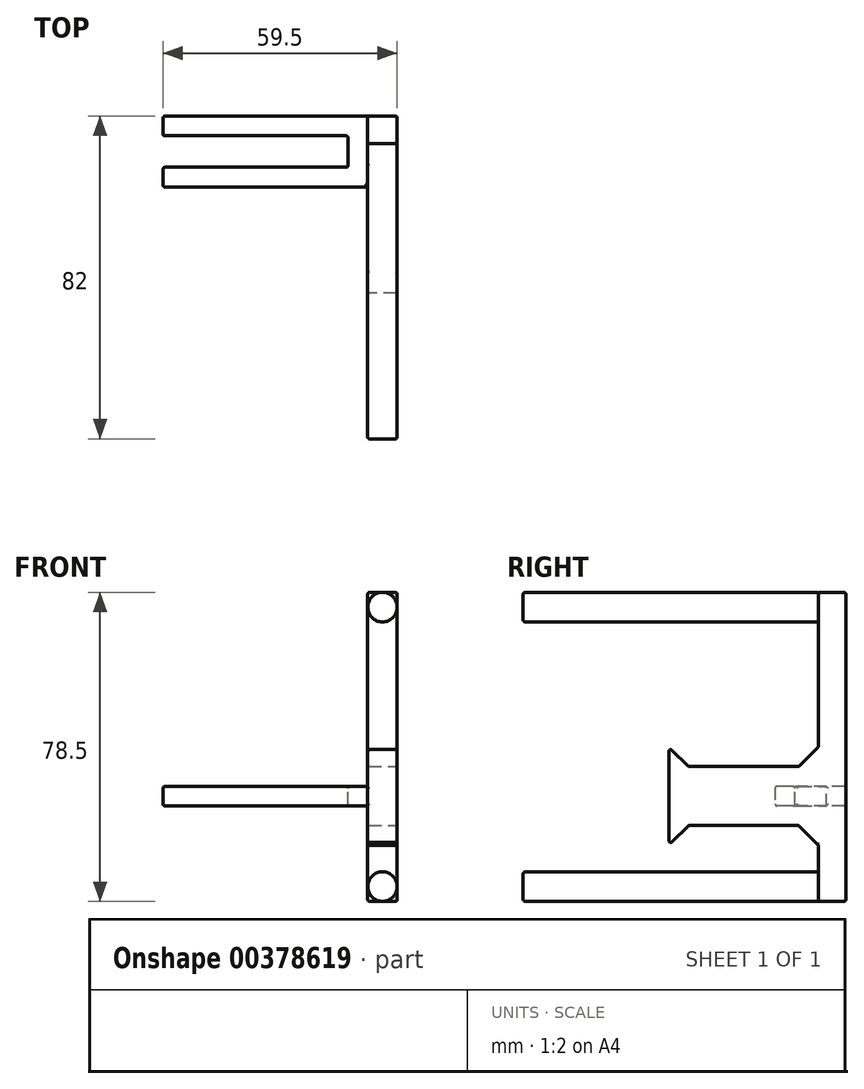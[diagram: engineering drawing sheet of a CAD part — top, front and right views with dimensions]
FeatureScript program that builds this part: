
annotation { "Feature Type Name" : "Feature", "Feature Type Description" : "" }
export const myFeature = defineFeature(function(context is Context, id is Id, definition is map)
    precondition{}
    {
        {
            var Q0;
            Q0=qCreatedBy(makeId("Front.planeOp"),FACE);
            var sketch = newSketch(context, id + "F0", { "sketchPlane" : qUnion([Q0])});
            skLineSegment(sketch, "E0", {"start": v(0, 35.5) * mm, "end": v(0, -35.5) * mm, "construction": true});
            skCircle(sketch, "E1", {"center": v(0, 35.5) * mm, "radius": 3.75 * mm});
            skCircle(sketch, "E2.MirrorC", {"center": v(0, -35.5) * mm, "radius": 3.75 * mm});
            skSolve(sketch);
        }
        {
            var Q0;
            Q0 = qSketchRegion(id + "F0", true);
            extrude(context, id + "F1", {"entities" : qUnion([Q0]), "depth" : 75 * mm});
        }
        {
            var Q0;
            Q0=qCreatedBy(makeId("Front.planeOp"),FACE);
            var sketch = newSketch(context, id + "F2", { "sketchPlane" : qUnion([Q0])});
            skLineSegment(sketch, "E3.bottom", {"start": v(3.75, 39.25) * mm, "end": v(-3.75, 39.25) * mm});
            skLineSegment(sketch, "E3.top", {"start": v(3.75, -39.25) * mm, "end": v(-3.75, -39.25) * mm});
            skLineSegment(sketch, "E3.left", {"start": v(3.75, 39.25) * mm, "end": v(3.75, -39.25) * mm});
            skLineSegment(sketch, "E3.right", {"start": v(-3.75, 39.25) * mm, "end": v(-3.75, -39.25) * mm});
            skSolve(sketch);
        }
        {
            var Q0;
            Q0 = qSketchRegion(id + "F2", true);
            extrude(context, id + "F3", {"entities" : qUnion([Q0]), "oppositeDirection" : true, "depth" : 7 * mm});
        }
        {
            var Q0;
            Q0=makeQuery(id+"F3.opExtrude","CAP_FACE",FACE,{"disambiguationData":[OSD([sQuery(id+"F2.wireOp",EDGE,"E3.bottom"),sQuery(id+"F2.wireOp",EDGE,"E3.top"),sQuery(id+"F2.wireOp",EDGE,"E3.left"),sQuery(id+"F2.wireOp",EDGE,"E3.right")])],"isStart":false});
            var sketch = newSketch(context, id + "F4", { "sketchPlane" : qUnion([Q0])});
            skLineSegment(sketch, "E4.bottom", {"start": v(-3.75, 0) * mm, "end": v(3.75, 0) * mm});
            skLineSegment(sketch, "E4.top", {"start": v(-3.75, -25) * mm, "end": v(3.75, -25) * mm});
            skLineSegment(sketch, "E4.left", {"start": v(-3.75, 0) * mm, "end": v(-3.75, -25) * mm});
            skLineSegment(sketch, "E4.right", {"start": v(3.75, 0) * mm, "end": v(3.75, -25) * mm});
            skSolve(sketch);
        }
        {
            var Q0;
            Q0 = qSketchRegion(id + "F4", true);
            extrude(context, id + "F5", {"entities" : qUnion([Q0]), "operationType" : NewBodyOperationType.ADD, "oppositeDirection" : true, "depth" : 45 * mm});
        }
        {
            var Q0;
            Q0=makeQuery(id+"F5.boolean.opBoolean","MERGE",FACE,{"derivedFrom":[makeQuery(id+"F3.opExtrude","SWEPT_FACE",FACE,{"disambiguationData":[OSD([sQuery(id+"F2.wireOp",EDGE,"E3.left")])]}),makeQuery(id+"F5.opExtrude","SWEPT_FACE",FACE,{"disambiguationData":[OSD([sQuery(id+"F4.wireOp",EDGE,"E4.left")])]})]});
            var sketch = newSketch(context, id + "F6", { "sketchPlane" : qUnion([Q0])});
            skLineSegment(sketch, "E5", {"start": v(-38, 0) * mm, "end": v(-33, -5) * mm});
            skLineSegment(sketch, "E6", {"start": v(-33, -5) * mm, "end": v(-5, -5) * mm});
            skLineSegment(sketch, "E7", {"start": v(-5, -5) * mm, "end": v(0, 0) * mm});
            skLineSegment(sketch, "E8", {"start": v(-38, -12.5) * mm, "end": v(7, -12.5) * mm, "construction": true});
            skLineSegment(sketch, "E9.MirrorCS", {"start": v(-38, -25) * mm, "end": v(-33, -20) * mm});
            skLineSegment(sketch, "E10.MirrorCS", {"start": v(-33, -20) * mm, "end": v(-5, -20) * mm});
            skLineSegment(sketch, "E11.MirrorCS", {"start": v(-5, -20) * mm, "end": v(0, -25) * mm});
            skLineSegment(sketch, "E12", {"start": v(-38, 0) * mm, "end": v(0, 0) * mm});
            skLineSegment(sketch, "E13", {"start": v(0, -25) * mm, "end": v(-38, -25) * mm});
            skSolve(sketch);
        }
        {
            var Q0;
            Q0 = qSketchRegion(id + "F6", true);
            var Q1;
            Q1=makeQuery(id+"F5.boolean.opBoolean","MERGE",FACE,{"derivedFrom":[makeQuery(id+"F3.opExtrude","SWEPT_FACE",FACE,{"disambiguationData":[OSD([sQuery(id+"F2.wireOp",EDGE,"E3.right")])]}),makeQuery(id+"F5.opExtrude","SWEPT_FACE",FACE,{"disambiguationData":[OSD([sQuery(id+"F4.wireOp",EDGE,"E4.right")])]})]});
            extrude(context, id + "F7", {"entities" : qUnion([Q0]), "operationType" : NewBodyOperationType.REMOVE, "oppositeDirection" : true, "endBoundEntityFace" : qUnion([Q1]), "depth" : 25 * mm});
        }
        {
            var Q0;
            Q0=makeQuery(id+"F5.boolean.opBoolean","MERGE",FACE,{"derivedFrom":[makeQuery(id+"F3.opExtrude","SWEPT_FACE",FACE,{"disambiguationData":[OSD([sQuery(id+"F2.wireOp",EDGE,"E3.right")])]}),makeQuery(id+"F5.opExtrude","SWEPT_FACE",FACE,{"disambiguationData":[OSD([sQuery(id+"F4.wireOp",EDGE,"E4.right")])]})]});
            var sketch = newSketch(context, id + "F8", { "sketchPlane" : qUnion([Q0])});
            skLineSegment(sketch, "E14", {"start": v(38, -12.5) * mm, "end": v(-7, -12.5) * mm, "construction": true});
            skLineSegment(sketch, "E15.bottom", {"start": v(-7, -10) * mm, "end": v(11, -10) * mm});
            skLineSegment(sketch, "E15.top", {"start": v(-7, -15) * mm, "end": v(11, -15) * mm});
            skLineSegment(sketch, "E15.left", {"start": v(-7, -10) * mm, "end": v(-7, -15) * mm});
            skLineSegment(sketch, "E15.right", {"start": v(11, -10) * mm, "end": v(11, -15) * mm});
            skSolve(sketch);
        }
        {
            var Q0;
            Q0 = qSketchRegion(id + "F8", true);
            extrude(context, id + "F9", {"entities" : qUnion([Q0]), "operationType" : NewBodyOperationType.ADD, "depth" : 52 * mm});
        }
        {
            var Q0;
            Q0=makeQuery(id+"F9.opExtrude","SWEPT_FACE",FACE,{"disambiguationData":[OSD([sQuery(id+"F8.wireOp",EDGE,"E15.bottom")])]});
            var sketch = newSketch(context, id + "F10", { "sketchPlane" : qUnion([Q0])});
            skLineSegment(sketch, "E16.0", {"start": v(-8.75, -6) * mm, "end": v(-8.75, 2) * mm});
            skLineSegment(sketch, "E16.1", {"start": v(-55.75, -6) * mm, "end": v(-8.75, -6) * mm});
            skLineSegment(sketch, "E16.2", {"start": v(-55.75, 2) * mm, "end": v(-55.75, -6) * mm});
            skLineSegment(sketch, "E16.3", {"start": v(-8.75, 2) * mm, "end": v(-55.75, 2) * mm});
            skSolve(sketch);
        }
        {
            var Q0;
            Q0=makeQuery(id+"F10.imprint","IMPRINT",FACE,{"disambiguationData":[TD([[makeQuery(id+"F10.imprint","IMPRINT",EDGE,{"derivedFrom":sQuery(id+"F10.wireOp",EDGE,"E16.0")}),1.0]])]});
            extrude(context, id + "F11", {"entities" : qUnion([Q0]), "operationType" : NewBodyOperationType.REMOVE, "oppositeDirection" : true, "depth" : 25 * mm});
        }
        {
            var Q0;
            Q0=makeQuery(id+"F11.boolean.opBoolean","COPY",EDGE,{"derivedFrom":makeQuery(id+"F11.opExtrude","SWEPT_EDGE",EDGE,{"disambiguationData":[OSD([sQuery(id+"F10.wireOp",EDGE,"E16.2"),sQuery(id+"F10.wireOp",EDGE,"E16.3")])]})});
            var Q1;
            Q1=makeQuery(id+"F11.boolean.opBoolean","COPY",EDGE,{"derivedFrom":makeQuery(id+"F11.opExtrude","SWEPT_EDGE",EDGE,{"disambiguationData":[OSD([sQuery(id+"F10.wireOp",EDGE,"E16.1"),sQuery(id+"F10.wireOp",EDGE,"E16.2")])]})});
            var Q2;
            Q2=makeQuery(id+"F11.boolean.opBoolean","COPY",EDGE,{"derivedFrom":makeQuery(id+"F11.opExtrude","SWEPT_EDGE",EDGE,{"disambiguationData":[OSD([sQuery(id+"F10.wireOp",EDGE,"E16.0"),sQuery(id+"F10.wireOp",EDGE,"E16.3")])]})});
            var Q3;
            Q3=makeQuery(id+"F3.opExtrude","SWEPT_EDGE",EDGE,{"disambiguationData":[OSD([sQuery(id+"F2.wireOp",EDGE,"E3.top"),sQuery(id+"F2.wireOp",EDGE,"E3.right")])]});
            var Q4;
            Q4=makeQuery(id+"F3.opExtrude","CAP_EDGE",EDGE,{"disambiguationData":[OSD([sQuery(id+"F2.wireOp",EDGE,"E3.top")])],"isStart":false});
            var Q5;
            Q5=makeQuery(id+"F3.opExtrude","SWEPT_EDGE",EDGE,{"disambiguationData":[OSD([sQuery(id+"F2.wireOp",EDGE,"E3.top"),sQuery(id+"F2.wireOp",EDGE,"E3.left")])]});
            var Q6;
            {var subQ0=sQuery(id+"F2.wireOp",EDGE,"E3.right");var subQ1=sQuery(id+"F2.wireOp",EDGE,"E3.top");Q6=makeQuery(id+"F9.boolean.opBoolean","SPLIT",EDGE,{"disambiguationData":[TD([makeQuery(id+"F3.opExtrude","SWEPT_FACE",FACE,{"disambiguationData":[OSD([subQ1])]})])],"derivedFrom":makeQuery(id+"F3.opExtrude","CAP_EDGE",EDGE,{"disambiguationData":[OSD([subQ0])],"isStart":false})});}
            var Q7;
            Q7=makeQuery(id+"F3.opExtrude","CAP_EDGE",EDGE,{"disambiguationData":[OSD([sQuery(id+"F2.wireOp",EDGE,"E3.left")])],"isStart":false});
            var Q8;
            Q8=makeQuery(id+"F9.opExtrude","SWEPT_EDGE",EDGE,{"disambiguationData":[OSD([sQuery(id+"F2.wireOp",EDGE,"E3.right"),sQuery(id+"F8.wireOp",EDGE,"E15.top"),sQuery(id+"F8.wireOp",EDGE,"E15.left")])]});
            var Q9;
            Q9=makeQuery(id+"F9.opExtrude","SWEPT_EDGE",EDGE,{"disambiguationData":[OSD([sQuery(id+"F2.wireOp",EDGE,"E3.right"),sQuery(id+"F8.wireOp",EDGE,"E15.bottom"),sQuery(id+"F8.wireOp",EDGE,"E15.left")])]});
            var Q10;
            {var subQ0=sQuery(id+"F2.wireOp",EDGE,"E3.right");var subQ1=sQuery(id+"F2.wireOp",EDGE,"E3.bottom");Q10=makeQuery(id+"F9.boolean.opBoolean","SPLIT",EDGE,{"disambiguationData":[TD([makeQuery(id+"F3.opExtrude","SWEPT_FACE",FACE,{"disambiguationData":[OSD([subQ1])]})])],"derivedFrom":makeQuery(id+"F3.opExtrude","CAP_EDGE",EDGE,{"disambiguationData":[OSD([subQ0])],"isStart":false})});}
            var Q11;
            Q11=makeQuery(id+"F7.boolean.opBoolean","COPY",EDGE,{"derivedFrom":makeQuery(id+"F7.opExtrude","CAP_EDGE",EDGE,{"disambiguationData":[OSD([sQuery(id+"F6.wireOp",EDGE,"E10.MirrorCS")])],"isStart":true})});
            var Q12;
            Q12=makeQuery(id+"F7.boolean.opBoolean","COPY",EDGE,{"derivedFrom":makeQuery(id+"F7.opExtrude","CAP_EDGE",EDGE,{"disambiguationData":[OSD([sQuery(id+"F6.wireOp",EDGE,"E11.MirrorCS")])],"isStart":true})});
            var Q13;
            Q13=makeQuery(id+"F7.boolean.opBoolean","INTERSECT",EDGE,{"derivedFrom":[makeQuery(id+"F5.boolean.opBoolean","MERGE",FACE,{"derivedFrom":[makeQuery(id+"F3.opExtrude","SWEPT_FACE",FACE,{"disambiguationData":[OSD([sQuery(id+"F2.wireOp",EDGE,"E3.right")])]}),makeQuery(id+"F5.opExtrude","SWEPT_FACE",FACE,{"disambiguationData":[OSD([sQuery(id+"F4.wireOp",EDGE,"E4.right")])]})]}),makeQuery(id+"F7.opExtrude","SWEPT_FACE",FACE,{"disambiguationData":[OSD([sQuery(id+"F6.wireOp",EDGE,"E11.MirrorCS")])]})]});
            var Q14;
            Q14=makeQuery(id+"F7.boolean.opBoolean","INTERSECT",EDGE,{"derivedFrom":[makeQuery(id+"F5.boolean.opBoolean","MERGE",FACE,{"derivedFrom":[makeQuery(id+"F3.opExtrude","SWEPT_FACE",FACE,{"disambiguationData":[OSD([sQuery(id+"F2.wireOp",EDGE,"E3.right")])]}),makeQuery(id+"F5.opExtrude","SWEPT_FACE",FACE,{"disambiguationData":[OSD([sQuery(id+"F4.wireOp",EDGE,"E4.right")])]})]}),makeQuery(id+"F7.opExtrude","SWEPT_FACE",FACE,{"disambiguationData":[OSD([sQuery(id+"F6.wireOp",EDGE,"E10.MirrorCS")])]})]});
            var Q15;
            Q15=makeQuery(id+"F7.boolean.opBoolean","COPY",EDGE,{"derivedFrom":makeQuery(id+"F7.opExtrude","SWEPT_EDGE",EDGE,{"disambiguationData":[OSD([sQuery(id+"F6.wireOp",EDGE,"E10.MirrorCS"),sQuery(id+"F6.wireOp",EDGE,"E11.MirrorCS")])]})});
            var Q16;
            {var subQ0=sQuery(id+"F2.wireOp",EDGE,"E3.left");Q16=makeQuery(id+"F7.boolean.opBoolean","MERGE",EDGE,{"derivedFrom":[makeQuery(id+"F5.boolean.opBoolean","INTERSECT",EDGE,{"derivedFrom":[makeQuery(id+"F3.opExtrude","CAP_FACE",FACE,{"disambiguationData":[OSD([sQuery(id+"F2.wireOp",EDGE,"E3.bottom"),sQuery(id+"F2.wireOp",EDGE,"E3.top"),subQ0,sQuery(id+"F2.wireOp",EDGE,"E3.right")])],"isStart":true}),makeQuery(id+"F5.opExtrude","SWEPT_FACE",FACE,{"disambiguationData":[OSD([sQuery(id+"F4.wireOp",EDGE,"E4.bottom")])]})]}),makeQuery(id+"F7.opExtrude","SWEPT_EDGE",EDGE,{"disambiguationData":[OSD([subQ0,sQuery(id+"F6.wireOp",EDGE,"E7"),sQuery(id+"F6.wireOp",EDGE,"E12")])]})]});}
            var Q17;
            Q17=makeQuery(id+"F7.boolean.opBoolean","COPY",EDGE,{"derivedFrom":makeQuery(id+"F7.opExtrude","SWEPT_EDGE",EDGE,{"disambiguationData":[OSD([sQuery(id+"F6.wireOp",EDGE,"E6"),sQuery(id+"F6.wireOp",EDGE,"E7")])]})});
            var Q18;
            Q18=makeQuery(id+"F7.boolean.opBoolean","COPY",EDGE,{"derivedFrom":makeQuery(id+"F7.opExtrude","CAP_EDGE",EDGE,{"disambiguationData":[OSD([sQuery(id+"F6.wireOp",EDGE,"E7")])],"isStart":true})});
            var Q19;
            Q19=makeQuery(id+"F7.boolean.opBoolean","COPY",EDGE,{"derivedFrom":makeQuery(id+"F7.opExtrude","CAP_EDGE",EDGE,{"disambiguationData":[OSD([sQuery(id+"F6.wireOp",EDGE,"E6")])],"isStart":true})});
            var Q20;
            Q20=makeQuery(id+"F7.boolean.opBoolean","INTERSECT",EDGE,{"derivedFrom":[makeQuery(id+"F5.boolean.opBoolean","MERGE",FACE,{"derivedFrom":[makeQuery(id+"F3.opExtrude","SWEPT_FACE",FACE,{"disambiguationData":[OSD([sQuery(id+"F2.wireOp",EDGE,"E3.right")])]}),makeQuery(id+"F5.opExtrude","SWEPT_FACE",FACE,{"disambiguationData":[OSD([sQuery(id+"F4.wireOp",EDGE,"E4.right")])]})]}),makeQuery(id+"F7.opExtrude","SWEPT_FACE",FACE,{"disambiguationData":[OSD([sQuery(id+"F6.wireOp",EDGE,"E7")])]})]});
            var Q21;
            {var subQ0=sQuery(id+"F2.wireOp",EDGE,"E3.right");var subQ1=sQuery(id+"F2.wireOp",EDGE,"E3.bottom");Q21=makeQuery(id+"F5.boolean.opBoolean","SPLIT",EDGE,{"disambiguationData":[TD([makeQuery(id+"F3.opExtrude","SWEPT_FACE",FACE,{"disambiguationData":[OSD([subQ1])]})])],"derivedFrom":makeQuery(id+"F3.opExtrude","CAP_EDGE",EDGE,{"disambiguationData":[OSD([subQ0])],"isStart":true})});}
            var Q22;
            Q22=makeQuery(id+"F7.boolean.opBoolean","INTERSECT",EDGE,{"derivedFrom":[makeQuery(id+"F5.boolean.opBoolean","MERGE",FACE,{"derivedFrom":[makeQuery(id+"F3.opExtrude","SWEPT_FACE",FACE,{"disambiguationData":[OSD([sQuery(id+"F2.wireOp",EDGE,"E3.right")])]}),makeQuery(id+"F5.opExtrude","SWEPT_FACE",FACE,{"disambiguationData":[OSD([sQuery(id+"F4.wireOp",EDGE,"E4.right")])]})]}),makeQuery(id+"F7.opExtrude","SWEPT_FACE",FACE,{"disambiguationData":[OSD([sQuery(id+"F6.wireOp",EDGE,"E5")])]})]});
            var Q23;
            Q23=makeQuery(id+"F9.opExtrude","SWEPT_FACE",FACE,{"disambiguationData":[OSD([sQuery(id+"F8.wireOp",EDGE,"E15.right")])]});
            var Q24;
            Q24=makeQuery(id+"F3.opExtrude","CAP_EDGE",EDGE,{"disambiguationData":[OSD([sQuery(id+"F2.wireOp",EDGE,"E3.bottom")])],"isStart":false});
            var Q25;
            Q25=makeQuery(id+"F3.opExtrude","SWEPT_EDGE",EDGE,{"disambiguationData":[OSD([sQuery(id+"F2.wireOp",EDGE,"E3.bottom"),sQuery(id+"F2.wireOp",EDGE,"E3.left")])]});
            var Q26;
            Q26=makeQuery(id+"F3.opExtrude","SWEPT_EDGE",EDGE,{"disambiguationData":[OSD([sQuery(id+"F2.wireOp",EDGE,"E3.bottom"),sQuery(id+"F2.wireOp",EDGE,"E3.right")])]});
            var Q27;
            Q27=makeQuery(id+"F7.boolean.opBoolean","MERGE",EDGE,{"derivedFrom":[makeQuery(id+"F5.opExtrude","CAP_EDGE",EDGE,{"disambiguationData":[OSD([sQuery(id+"F4.wireOp",EDGE,"E4.top")])],"isStart":false}),makeQuery(id+"F7.opExtrude","SWEPT_EDGE",EDGE,{"disambiguationData":[OSD([sQuery(id+"F4.wireOp",EDGE,"E4.left"),sQuery(id+"F6.wireOp",EDGE,"E9.MirrorCS"),sQuery(id+"F6.wireOp",EDGE,"E13")])]})]});
            var Q28;
            Q28=makeQuery(id+"F5.opExtrude","CAP_FACE",FACE,{"disambiguationData":[OSD([sQuery(id+"F4.wireOp",EDGE,"E4.bottom"),sQuery(id+"F4.wireOp",EDGE,"E4.top"),sQuery(id+"F4.wireOp",EDGE,"E4.left"),sQuery(id+"F4.wireOp",EDGE,"E4.right")])],"isStart":false});
            var Q29;
            Q29=makeQuery(id+"F7.boolean.opBoolean","COPY",FACE,{"derivedFrom":makeQuery(id+"F7.opExtrude","SWEPT_FACE",FACE,{"disambiguationData":[OSD([sQuery(id+"F6.wireOp",EDGE,"E9.MirrorCS")])]})});
            var Q30;
            Q30=makeQuery(id+"F7.boolean.opBoolean","COPY",FACE,{"derivedFrom":makeQuery(id+"F7.opExtrude","SWEPT_FACE",FACE,{"disambiguationData":[OSD([sQuery(id+"F6.wireOp",EDGE,"E5")])]})});
            var Q31;
            Q31=makeQuery(id+"F9.opExtrude","CAP_FACE",FACE,{"disambiguationData":[OSD([sQuery(id+"F8.wireOp",EDGE,"E15.bottom"),sQuery(id+"F8.wireOp",EDGE,"E15.top"),sQuery(id+"F8.wireOp",EDGE,"E15.left"),sQuery(id+"F8.wireOp",EDGE,"E15.right")])],"isStart":false});
            var Q32;
            Q32=makeQuery(id+"F11.boolean.opBoolean","COPY",FACE,{"derivedFrom":makeQuery(id+"F11.opExtrude","SWEPT_FACE",FACE,{"disambiguationData":[OSD([sQuery(id+"F10.wireOp",EDGE,"E16.2")])]})});
            var Q33;
            Q33=makeQuery(id+"F11.boolean.opBoolean","COPY",FACE,{"derivedFrom":makeQuery(id+"F11.opExtrude","SWEPT_FACE",FACE,{"disambiguationData":[OSD([sQuery(id+"F10.wireOp",EDGE,"E16.1")])]})});
            var Q34;
            Q34=makeQuery(id+"F1.opExtrude","CAP_EDGE",EDGE,{"disambiguationData":[OSD([sQuery(id+"F0.wireOp",EDGE,"E2.MirrorC")])],"isStart":false});
            var Q35;
            Q35=makeQuery(id+"F1.opExtrude","CAP_EDGE",EDGE,{"disambiguationData":[OSD([sQuery(id+"F0.wireOp",EDGE,"E1")])],"isStart":false});
            var Q36;
            Q36=makeQuery(id+"F1.opExtrude","SWEPT_FACE",FACE,{"disambiguationData":[OSD([sQuery(id+"F0.wireOp",EDGE,"E1")])]});
            fillet(context, id + "F12", {"entities" : qUnion([Q0, Q1, Q2, Q3, Q4, Q5, Q6, Q7, Q8, Q9, Q10, Q11, Q12, Q13, Q14, Q15, Q16, Q17, Q18, Q19, Q20, Q21, Q22, Q23, Q24, Q25, Q26, Q27, Q28, Q29, Q30, Q31, Q32, Q33, Q34, Q35, Q36]), "radius" : 0.5 * mm, "tangentPropagation" : true, "allowEdgeOverflow" : false});
        }
    });
